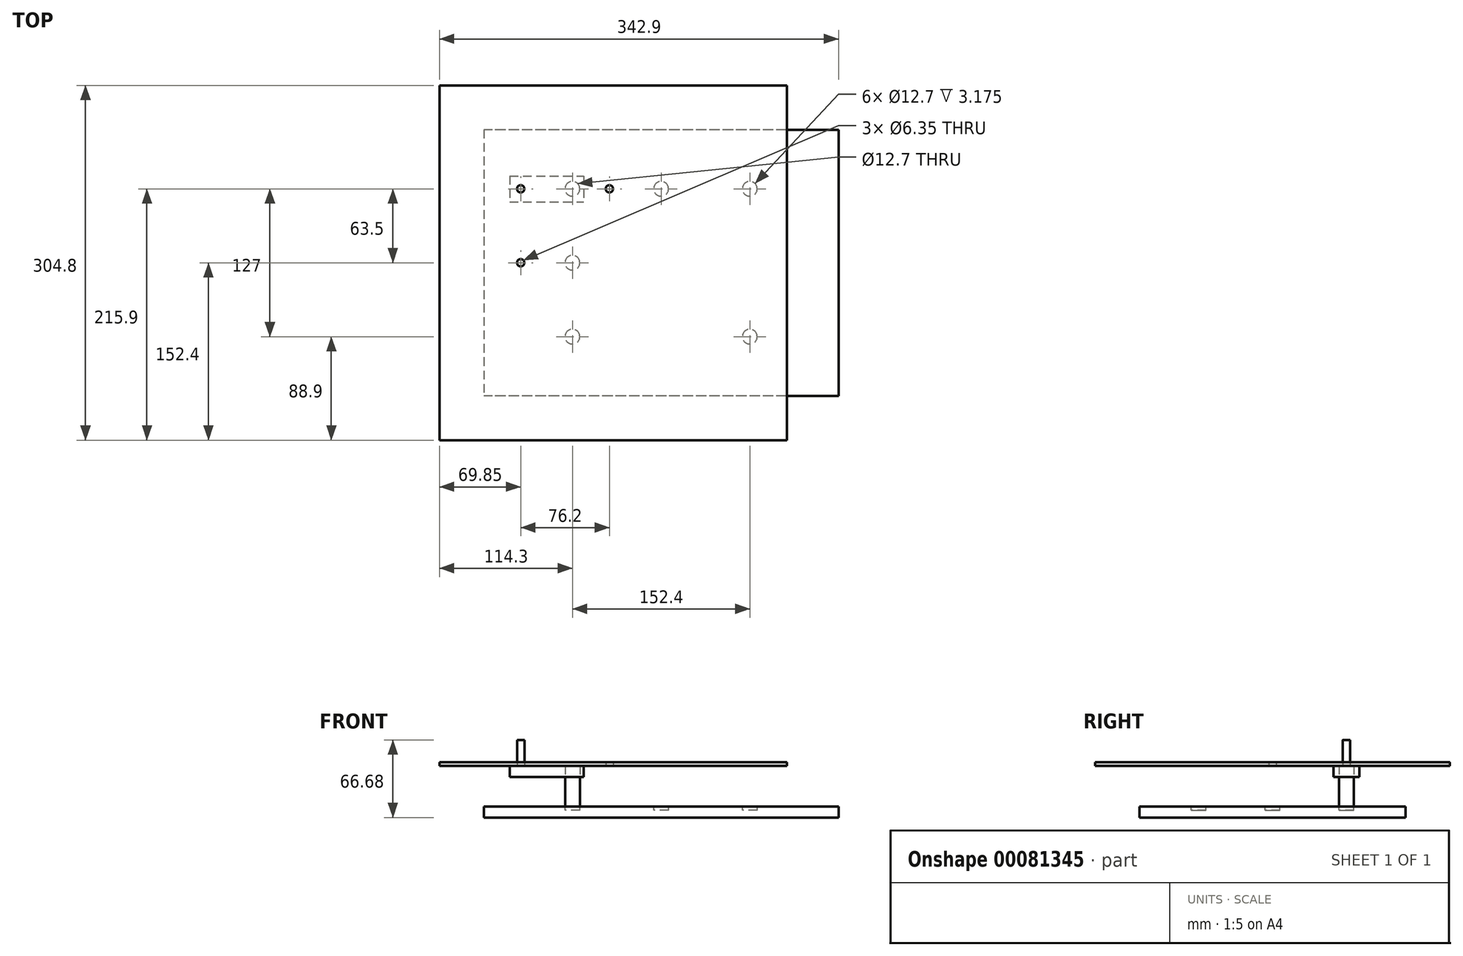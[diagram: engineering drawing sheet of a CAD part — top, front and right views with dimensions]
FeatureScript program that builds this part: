
annotation { "Feature Type Name" : "Feature", "Feature Type Description" : "" }
export const myFeature = defineFeature(function(context is Context, id is Id, definition is map)
    precondition{}
    {
        {
            var Q0;
            Q0=qCreatedBy(makeId("Top.planeOp"),FACE);
            var sketch = newSketch(context, id + "F0", { "sketchPlane" : qUnion([Q0])});
            skLineSegment(sketch, "E0.bottom", {"start": v(152.4, 114.3) * mm, "end": v(-152.4, 114.3) * mm});
            skLineSegment(sketch, "E0.top", {"start": v(152.4, -114.3) * mm, "end": v(-152.4, -114.3) * mm});
            skLineSegment(sketch, "E0.left", {"start": v(152.4, 114.3) * mm, "end": v(152.4, -114.3) * mm});
            skLineSegment(sketch, "E0.right", {"start": v(-152.4, 114.3) * mm, "end": v(-152.4, -114.3) * mm});
            skPoint(sketch, "E0.middle", {"position": v(0, 0) * mm});
            skSolve(sketch);
        }
        {
            var Q0;
            Q0 = qSketchRegion(id + "F0", true);
            extrude(context, id + "F1", {"entities" : qUnion([Q0]), "depth" : 9.52 * mm});
        }
        {
            var Q0;
            Q0=makeQuery(id+"F1.opExtrude","CAP_FACE",FACE,{"disambiguationData":[OSD([sQuery(id+"F0.wireOp",EDGE,"E0.bottom"),sQuery(id+"F0.wireOp",EDGE,"E0.top"),sQuery(id+"F0.wireOp",EDGE,"E0.left"),sQuery(id+"F0.wireOp",EDGE,"E0.right")])],"isStart":false});
            var sketch = newSketch(context, id + "F2", { "sketchPlane" : qUnion([Q0])});
            skCircle(sketch, "E1", {"center": v(-76.2, 63.5) * mm, "radius": 6.35 * mm});
            skCircle(sketch, "E2", {"center": v(76.2, 63.5) * mm, "radius": 6.35 * mm});
            skCircle(sketch, "E3", {"center": v(76.2, -63.5) * mm, "radius": 6.35 * mm});
            skCircle(sketch, "E4", {"center": v(-76.2, -63.5) * mm, "radius": 6.35 * mm});
            skSolve(sketch);
        }
        {
            var Q0;
            Q0=makeQuery(id+"F2.imprint","IMPRINT",FACE,{"disambiguationData":[TD([[makeQuery(id+"F2.imprint","IMPRINT",EDGE,{"derivedFrom":sQuery(id+"F2.wireOp",EDGE,"E1")}),1.0]])]});
            extrude(context, id + "F3", {"entities" : qUnion([Q0]), "depth" : 25.4 * mm});
        }
        {
            var Q0;
            Q0=makeQuery(id+"F2.imprint","IMPRINT",FACE,{"disambiguationData":[TD([[makeQuery(id+"F2.imprint","IMPRINT",EDGE,{"derivedFrom":sQuery(id+"F2.wireOp",EDGE,"E1")}),1.0]])]});
            var Q1;
            Q1=makeQuery(id+"F2.imprint","IMPRINT",FACE,{"disambiguationData":[TD([[makeQuery(id+"F2.imprint","IMPRINT",EDGE,{"derivedFrom":sQuery(id+"F2.wireOp",EDGE,"E4")}),1.0]])]});
            var Q2;
            Q2=makeQuery(id+"F2.imprint","IMPRINT",FACE,{"disambiguationData":[TD([[makeQuery(id+"F2.imprint","IMPRINT",EDGE,{"derivedFrom":sQuery(id+"F2.wireOp",EDGE,"E2")}),1.0]])]});
            var Q3;
            Q3=makeQuery(id+"F2.imprint","IMPRINT",FACE,{"disambiguationData":[TD([[makeQuery(id+"F2.imprint","IMPRINT",EDGE,{"derivedFrom":sQuery(id+"F2.wireOp",EDGE,"E3")}),1.0]])]});
            extrude(context, id + "F4", {"entities" : qUnion([Q0, Q1, Q2, Q3]), "operationType" : NewBodyOperationType.REMOVE, "oppositeDirection" : true, "depth" : 3.17 * mm});
        }
        {
            var Q0;
            Q0=makeQuery(id+"F2.imprint","IMPRINT",FACE,{"disambiguationData":[TD([[makeQuery(id+"F2.imprint","IMPRINT",EDGE,{"derivedFrom":sQuery(id+"F2.wireOp",EDGE,"E1")}),-1.0]])]});
            var sketch = newSketch(context, id + "F5", { "sketchPlane" : qUnion([Q0])});
            skPoint(sketch, "E5.0", {"position": v(-76.2, 63.5) * mm});
            skPoint(sketch, "E6.0", {"position": v(76.2, 63.5) * mm});
            skPoint(sketch, "E7.0", {"position": v(76.2, -63.5) * mm});
            skCircle(sketch, "E8", {"center": v(-76.2, 0) * mm, "radius": 6.35 * mm});
            skCircle(sketch, "E9", {"center": v(0, 63.5) * mm, "radius": 6.35 * mm});
            skSolve(sketch);
        }
        {
            var Q0;
            Q0 = qSketchRegion(id + "F5", true);
            extrude(context, id + "F6", {"entities" : qUnion([Q0]), "operationType" : NewBodyOperationType.REMOVE, "oppositeDirection" : true, "depth" : 3.17 * mm});
        }
        {
            var Q0;
            Q0=makeQuery(id+"F3.opExtrude","CAP_FACE",FACE,{"disambiguationData":[OSD([sQuery(id+"F2.wireOp",EDGE,"E1")])],"isStart":false});
            var sketch = newSketch(context, id + "F7", { "sketchPlane" : qUnion([Q0])});
            skCircle(sketch, "E10.0", {"center": v(-76.2, 63.5) * mm, "radius": 6.35 * mm});
            skLineSegment(sketch, "E11.bottom", {"start": v(-130.17, 74.61) * mm, "end": v(-66.67, 74.61) * mm});
            skLineSegment(sketch, "E11.top", {"start": v(-130.17, 52.39) * mm, "end": v(-66.67, 52.39) * mm});
            skLineSegment(sketch, "E11.left", {"start": v(-130.17, 74.61) * mm, "end": v(-130.17, 52.39) * mm});
            skLineSegment(sketch, "E11.right", {"start": v(-66.67, 74.61) * mm, "end": v(-66.67, 52.39) * mm});
            skLineSegment(sketch, "E12", {"start": v(-76.2, 74.61) * mm, "end": v(-76.2, 52.39) * mm});
            skSolve(sketch);
        }
        {
            var Q0;
            Q0 = qSketchRegion(id + "F7", true);
            extrude(context, id + "F8", {"entities" : qUnion([Q0]), "depth" : 9.52 * mm});
        }
        {
            var Q0;
            Q0=makeQuery(id+"F8.opExtrude","CAP_FACE",FACE,{"disambiguationData":[OSD([sQuery(id+"F7.wireOp",EDGE,"E10.0"),sQuery(id+"F7.wireOp",EDGE,"E11.bottom"),sQuery(id+"F7.wireOp",EDGE,"E11.top"),sQuery(id+"F7.wireOp",EDGE,"E11.left"),sQuery(id+"F7.wireOp",EDGE,"E11.right")])],"isStart":false});
            var sketch = newSketch(context, id + "F9", { "sketchPlane" : qUnion([Q0])});
            skCircle(sketch, "E13", {"center": v(-120.65, 63.5) * mm, "radius": 3.18 * mm});
            skPoint(sketch, "E13.centerSnap0", {"position": v(-130.17, 63.5) * mm});
            skCircle(sketch, "E14.0", {"center": v(-76.2, 63.5) * mm, "radius": 6.35 * mm});
            skSolve(sketch);
        }
        {
            var Q0;
            Q0=makeQuery(id+"F9.imprint","IMPRINT",FACE,{"disambiguationData":[TD([[makeQuery(id+"F9.imprint","IMPRINT",EDGE,{"derivedFrom":sQuery(id+"F9.wireOp",EDGE,"E13")}),1.0]])]});
            extrude(context, id + "F10", {"entities" : qUnion([Q0]), "operationType" : NewBodyOperationType.REMOVE, "oppositeDirection" : true, "depth" : 3.17 * mm});
        }
        {
            var Q0;
            Q0=makeQuery(id+"F10.boolean.opBoolean","COPY",FACE,{"derivedFrom":makeQuery(id+"F10.opExtrude","CAP_FACE",FACE,{"disambiguationData":[OSD([sQuery(id+"F9.wireOp",EDGE,"E13")])],"isStart":false})});
            extrude(context, id + "F11", {"entities" : qUnion([Q0]), "operationType" : NewBodyOperationType.ADD, "depth" : 25.4 * mm});
        }
        {
            var Q0;
            Q0=makeQuery(id+"F8.opExtrude","CAP_FACE",FACE,{"disambiguationData":[OSD([sQuery(id+"F7.wireOp",EDGE,"E10.0"),sQuery(id+"F7.wireOp",EDGE,"E11.bottom"),sQuery(id+"F7.wireOp",EDGE,"E11.top"),sQuery(id+"F7.wireOp",EDGE,"E11.left"),sQuery(id+"F7.wireOp",EDGE,"E11.right")])],"isStart":false});
            var sketch = newSketch(context, id + "F12", { "sketchPlane" : qUnion([Q0])});
            skLineSegment(sketch, "E15.0.0", {"start": v(152.4, -114.3) * mm, "end": v(152.4, 114.3) * mm});
            skLineSegment(sketch, "E15.0.1", {"start": v(152.4, 114.3) * mm, "end": v(-152.4, 114.3) * mm});
            skLineSegment(sketch, "E15.0.2", {"start": v(-152.4, 114.3) * mm, "end": v(-152.4, -114.3) * mm});
            skLineSegment(sketch, "E15.0.3", {"start": v(-152.4, -114.3) * mm, "end": v(152.4, -114.3) * mm});
            skCircle(sketch, "E16.0", {"center": v(0, 63.5) * mm, "radius": 6.35 * mm});
            skCircle(sketch, "E17.0", {"center": v(-76.2, 0) * mm, "radius": 6.35 * mm});
            skCircle(sketch, "E18", {"center": v(-44.45, 63.5) * mm, "radius": 3.18 * mm});
            skCircle(sketch, "E19", {"center": v(-120.65, 0) * mm, "radius": 3.18 * mm});
            skLineSegment(sketch, "E20.bottom", {"start": v(-190.5, -152.4) * mm, "end": v(190.5, -152.4) * mm});
            skLineSegment(sketch, "E20.top", {"start": v(-190.5, 152.4) * mm, "end": v(190.5, 152.4) * mm});
            skLineSegment(sketch, "E20.left", {"start": v(-190.5, -152.4) * mm, "end": v(-190.5, 152.4) * mm});
            skLineSegment(sketch, "E20.right", {"start": v(190.5, -152.4) * mm, "end": v(190.5, 152.4) * mm});
            skPoint(sketch, "E20.middle", {"position": v(0, 0) * mm});
            skLineSegment(sketch, "E21", {"start": v(107.95, -152.4) * mm, "end": v(107.95, 152.4) * mm});
            skSolve(sketch);
        }
        {
            var Q0;
            {var subQ5=sQuery(id+"F12.wireOp",EDGE,"E15.0.2");Q0=makeQuery(id+"F12.imprint","IMPRINT",FACE,{"disambiguationData":[TD([[makeQuery(id+"F12.imprint","IMPRINT",EDGE,{"derivedFrom":subQ5}),-1.0]])]});}
            var Q1;
            Q1=makeQuery(id+"F12.imprint","IMPRINT",FACE,{"disambiguationData":[TD([[makeQuery(id+"F12.imprint","IMPRINT",EDGE,{"derivedFrom":makeQuery(id+"F8.opExtrude","CAP_EDGE",EDGE,{"disambiguationData":[OSD([sQuery(id+"F7.wireOp",EDGE,"E10.0")])],"isStart":false})}),-1.0]])]});
            var Q2;
            {var subQ0=sQuery(id+"F12.wireOp",EDGE,"E15.0.2");Q2=makeQuery(id+"F12.imprint","IMPRINT",FACE,{"disambiguationData":[TD([[makeQuery(id+"F12.imprint","IMPRINT",EDGE,{"derivedFrom":subQ0}),1.0]])]});}
            var Q3;
            Q3=makeQuery(id+"F12.imprint","IMPRINT",FACE,{"disambiguationData":[TD([[makeQuery(id+"F12.imprint","IMPRINT",EDGE,{"derivedFrom":makeQuery(id+"F8.opExtrude","CAP_EDGE",EDGE,{"disambiguationData":[OSD([sQuery(id+"F7.wireOp",EDGE,"E10.0")])],"isStart":false})}),1.0]])]});
            var Q4;
            Q4=makeQuery(id+"F12.imprint","IMPRINT",FACE,{"disambiguationData":[TD([[makeQuery(id+"F12.imprint","IMPRINT",EDGE,{"derivedFrom":makeQuery(id+"F10.boolean.opBoolean","COPY",EDGE,{"derivedFrom":makeQuery(id+"F10.opExtrude","CAP_EDGE",EDGE,{"disambiguationData":[OSD([sQuery(id+"F9.wireOp",EDGE,"E13")])],"isStart":true})})}),1.0]])]});
            var Q5;
            Q5=makeQuery(id+"F12.imprint","IMPRINT",FACE,{"disambiguationData":[TD([[makeQuery(id+"F12.imprint","IMPRINT",EDGE,{"derivedFrom":sQuery(id+"F12.wireOp",EDGE,"E16.0")}),1.0]])]});
            var Q6;
            Q6=makeQuery(id+"F12.imprint","IMPRINT",FACE,{"disambiguationData":[TD([[makeQuery(id+"F12.imprint","IMPRINT",EDGE,{"derivedFrom":sQuery(id+"F12.wireOp",EDGE,"E17.0")}),1.0]])]});
            extrude(context, id + "F13", {"entities" : qUnion([Q0, Q1, Q2, Q3, Q4, Q5, Q6]), "depth" : 3.17 * mm});
        }
    });
